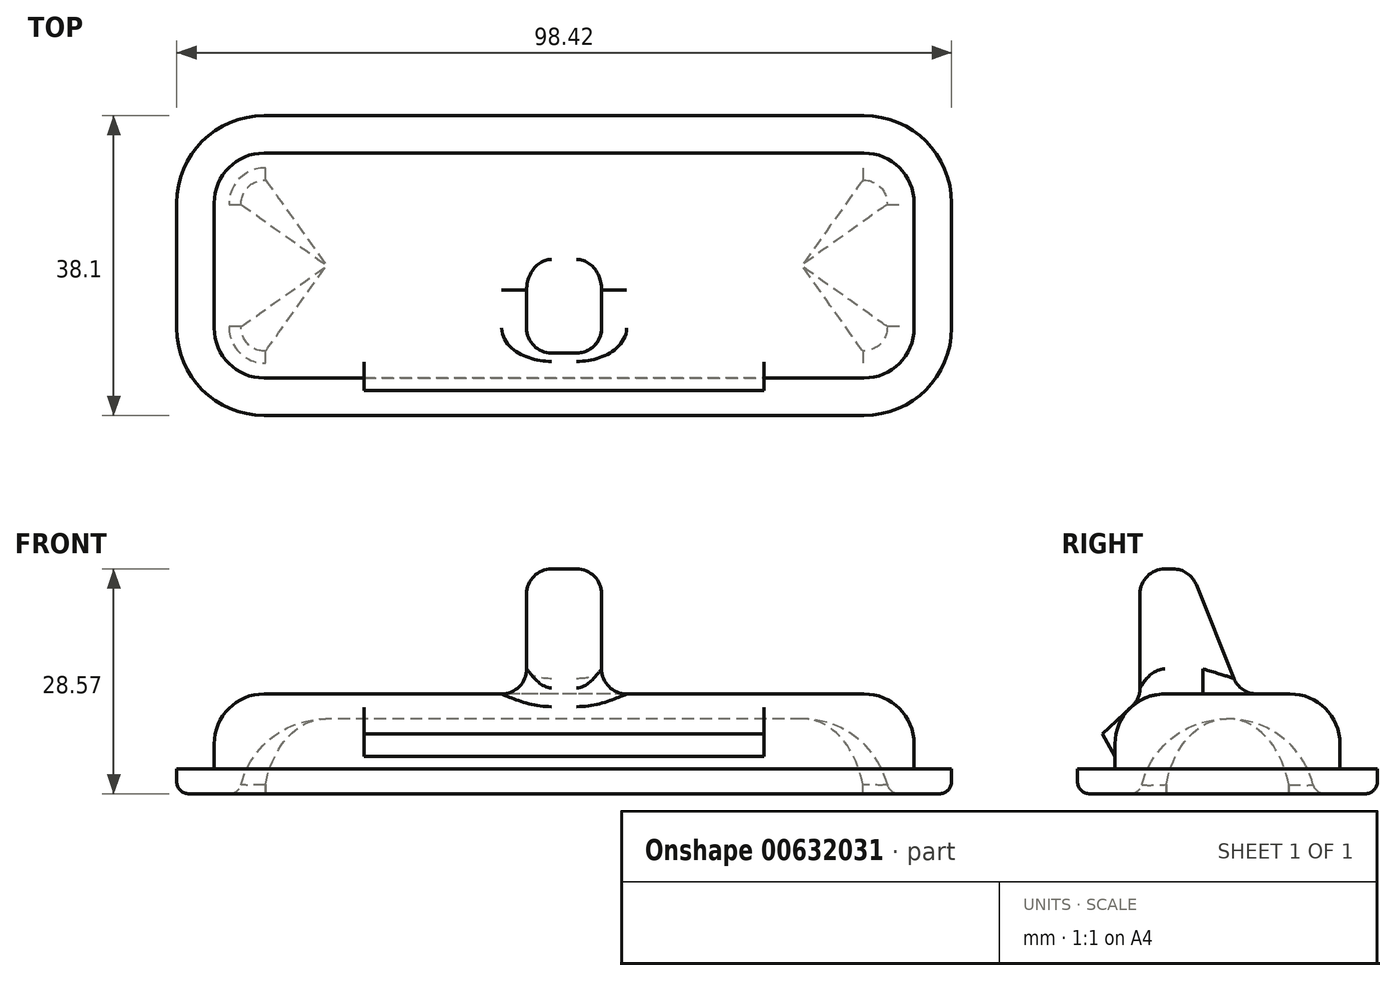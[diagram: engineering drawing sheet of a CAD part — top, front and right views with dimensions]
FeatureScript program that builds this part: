
annotation { "Feature Type Name" : "Feature", "Feature Type Description" : "" }
export const myFeature = defineFeature(function(context is Context, id is Id, definition is map)
    precondition{}
    {
        {
            var Q0;
            Q0=qCreatedBy(makeId("Top.planeOp"),FACE);
            var sketch = newSketch(context, id + "F0", { "sketchPlane" : qUnion([Q0])});
            skLineSegment(sketch, "E0.bottom", {"start": v(49.21, 19.05) * mm, "end": v(-49.21, 19.05) * mm});
            skLineSegment(sketch, "E0.top", {"start": v(49.21, -19.05) * mm, "end": v(-49.21, -19.05) * mm});
            skLineSegment(sketch, "E0.left", {"start": v(49.21, 19.05) * mm, "end": v(49.21, -19.05) * mm});
            skLineSegment(sketch, "E0.right", {"start": v(-49.21, 19.05) * mm, "end": v(-49.21, -19.05) * mm});
            skPoint(sketch, "E0.middle", {"position": v(0, 0) * mm});
            skSolve(sketch);
        }
        {
            var Q0;
            Q0=makeQuery(id+"F0.imprint","IMPRINT",FACE,{"disambiguationData":[TD([[makeQuery(id+"F0.imprint","IMPRINT",EDGE,{"derivedFrom":sQuery(id+"F0.wireOp",EDGE,"E0.bottom")}),1.0]])]});
            extrude(context, id + "F1", {"entities" : qUnion([Q0]), "depth" : 3.17 * mm, "offsetDistance" : 25.4 * mm});
        }
        {
            var Q0;
            Q0=makeQuery(id+"F1.opExtrude","CAP_FACE",FACE,{"disambiguationData":[OSD([sQuery(id+"F0.wireOp",EDGE,"E0.bottom"),sQuery(id+"F0.wireOp",EDGE,"E0.top"),sQuery(id+"F0.wireOp",EDGE,"E0.left"),sQuery(id+"F0.wireOp",EDGE,"E0.right")])],"isStart":false});
            var sketch = newSketch(context, id + "F2", { "sketchPlane" : qUnion([Q0])});
            skLineSegment(sketch, "E1.bottom", {"start": v(44.45, 14.29) * mm, "end": v(-44.45, 14.29) * mm});
            skLineSegment(sketch, "E1.top", {"start": v(44.45, -14.29) * mm, "end": v(-44.45, -14.29) * mm});
            skLineSegment(sketch, "E1.left", {"start": v(44.45, 14.29) * mm, "end": v(44.45, -14.29) * mm});
            skLineSegment(sketch, "E1.right", {"start": v(-44.45, 14.29) * mm, "end": v(-44.45, -14.29) * mm});
            skPoint(sketch, "E1.middle", {"position": v(0, 0) * mm});
            skSolve(sketch);
        }
        {
            var Q0;
            Q0=makeQuery(id+"F2.imprint","IMPRINT",FACE,{"disambiguationData":[TD([[makeQuery(id+"F2.imprint","IMPRINT",EDGE,{"derivedFrom":sQuery(id+"F2.wireOp",EDGE,"E1.bottom")}),1.0]])]});
            extrude(context, id + "F3", {"entities" : qUnion([Q0]), "operationType" : NewBodyOperationType.ADD, "depth" : 9.52 * mm, "offsetDistance" : 25.4 * mm});
        }
        {
            var Q0;
            Q0=makeQuery(id+"F1.opExtrude","SWEPT_EDGE",EDGE,{"disambiguationData":[OSD([sQuery(id+"F0.wireOp",EDGE,"E0.bottom"),sQuery(id+"F0.wireOp",EDGE,"E0.left")])]});
            var Q1;
            Q1=makeQuery(id+"F1.opExtrude","SWEPT_EDGE",EDGE,{"disambiguationData":[OSD([sQuery(id+"F0.wireOp",EDGE,"E0.top"),sQuery(id+"F0.wireOp",EDGE,"E0.left")])]});
            var Q2;
            Q2=makeQuery(id+"F1.opExtrude","SWEPT_EDGE",EDGE,{"disambiguationData":[OSD([sQuery(id+"F0.wireOp",EDGE,"E0.top"),sQuery(id+"F0.wireOp",EDGE,"E0.right")])]});
            var Q3;
            Q3=makeQuery(id+"F1.opExtrude","SWEPT_EDGE",EDGE,{"disambiguationData":[OSD([sQuery(id+"F0.wireOp",EDGE,"E0.bottom"),sQuery(id+"F0.wireOp",EDGE,"E0.right")])]});
            fillet(context, id + "F4", {"entities" : qUnion([Q0, Q1, Q2, Q3]), "radius" : 11.1 * mm, "tangentPropagation" : true, "allowEdgeOverflow" : false});
        }
        {
            var Q0;
            Q0=makeQuery(id+"F3.opExtrude","SWEPT_EDGE",EDGE,{"disambiguationData":[OSD([sQuery(id+"F2.wireOp",EDGE,"E1.top"),sQuery(id+"F2.wireOp",EDGE,"E1.left")])]});
            var Q1;
            Q1=makeQuery(id+"F3.opExtrude","SWEPT_EDGE",EDGE,{"disambiguationData":[OSD([sQuery(id+"F2.wireOp",EDGE,"E1.bottom"),sQuery(id+"F2.wireOp",EDGE,"E1.left")])]});
            var Q2;
            Q2=makeQuery(id+"F3.opExtrude","SWEPT_EDGE",EDGE,{"disambiguationData":[OSD([sQuery(id+"F2.wireOp",EDGE,"E1.bottom"),sQuery(id+"F2.wireOp",EDGE,"E1.right")])]});
            var Q3;
            Q3=makeQuery(id+"F3.opExtrude","SWEPT_EDGE",EDGE,{"disambiguationData":[OSD([sQuery(id+"F2.wireOp",EDGE,"E1.top"),sQuery(id+"F2.wireOp",EDGE,"E1.right")])]});
            fillet(context, id + "F5", {"entities" : qUnion([Q0, Q1, Q2, Q3]), "radius" : 6.35 * mm, "tangentPropagation" : true, "allowEdgeOverflow" : false});
        }
        {
            var Q0;
            Q0=makeQuery(id+"F1.opExtrude","CAP_FACE",FACE,{"disambiguationData":[OSD([sQuery(id+"F0.wireOp",EDGE,"E0.bottom"),sQuery(id+"F0.wireOp",EDGE,"E0.top"),sQuery(id+"F0.wireOp",EDGE,"E0.left"),sQuery(id+"F0.wireOp",EDGE,"E0.right")])],"isStart":true});
            shell(context, id + "F6", {"entities" : qUnion([Q0]), "thickness" : 3.17 * mm});
        }
        {
            var Q0;
            Q0=makeQuery(id+"F3.opExtrude","CAP_EDGE",EDGE,{"disambiguationData":[OSD([sQuery(id+"F2.wireOp",EDGE,"E1.top")])],"isStart":false});
            fillet(context, id + "F7", {"entities" : qUnion([Q0]), "radius" : 6.35 * mm, "tangentPropagation" : true, "allowEdgeOverflow" : false});
        }
        {
            var Q0;
            Q0=qCreatedBy(makeId("Right.planeOp"),FACE);
            var sketch = newSketch(context, id + "F8", { "sketchPlane" : qUnion([Q0])});
            skLineSegment(sketch, "E2", {"start": v(1.59, 12.7) * mm, "end": v(-4.76, 28.58) * mm});
            skLineSegment(sketch, "E3", {"start": v(-4.76, 28.58) * mm, "end": v(-11.11, 28.58) * mm});
            skLineSegment(sketch, "E4", {"start": v(-11.11, 11.85) * mm, "end": v(-11.11, 28.58) * mm});
            skArc(sketch, "E5.0", {"start": v(-7.94, 12.7) * mm, "mid": v(-9.58, 12.48) * mm, "end": v(-11.11, 11.85) * mm});
            skLineSegment(sketch, "E6.0", {"start": v(-7.94, 12.7) * mm, "end": v(1.59, 12.7) * mm});
            skPoint(sketch, "E7.orphan", {"position": v(-14.29, 6.35) * mm});
            skPoint(sketch, "E8.orphan", {"position": v(7.94, 12.7) * mm});
            skSolve(sketch);
        }
        {
            var Q0;
            Q0=qCreatedBy(makeId("Right.planeOp"),FACE);
            var sketch = newSketch(context, id + "F9", { "sketchPlane" : qUnion([Q0])});
            skLineSegment(sketch, "E9.0", {"start": v(-14.29, 3.18) * mm, "end": v(-14.29, 6.35) * mm});
            skLineSegment(sketch, "E10", {"start": v(-14.29, 4.76) * mm, "end": v(-15.88, 7.62) * mm});
            skLineSegment(sketch, "E11", {"start": v(-15.88, 7.62) * mm, "end": v(-15.88, 7.62) * mm});
            skLineSegment(sketch, "E12", {"start": v(-15.88, 7.62) * mm, "end": v(-12.28, 10.99) * mm});
            skPoint(sketch, "E13", {"position": v(-14.29, 4.76) * mm});
            skLineSegment(sketch, "E14", {"start": v(-15.88, 7.62) * mm, "end": v(-15.88, 11.92) * mm, "construction": true});
            skArc(sketch, "E15.0", {"start": v(-7.94, 12.7) * mm, "mid": v(-12.43, 10.84) * mm, "end": v(-14.29, 6.35) * mm});
            skSolve(sketch);
        }
        {
            var Q0;
            {var subQ3=sQuery(id+"F9.wireOp",EDGE,"E10");Q0=makeQuery(id+"F9.imprint","IMPRINT",FACE,{"disambiguationData":[TD([[makeQuery(id+"F9.imprint","IMPRINT",EDGE,{"derivedFrom":subQ3}),-1.0]])]});}
            extrude(context, id + "F10", {"entities" : qUnion([Q0]), "operationType" : NewBodyOperationType.ADD, "endBound" : BoundingType.SYMMETRIC, "oppositeDirection" : true, "depth" : 50.8 * mm, "offsetDistance" : 25.4 * mm});
        }
        {
            var Q0;
            Q0=makeQuery(id+"F8.imprint","IMPRINT",FACE,{"disambiguationData":[TD([[makeQuery(id+"F8.imprint","IMPRINT",EDGE,{"derivedFrom":sQuery(id+"F8.wireOp",EDGE,"E2")}),1.0]])]});
            extrude(context, id + "F11", {"entities" : qUnion([Q0]), "operationType" : NewBodyOperationType.ADD, "endBound" : BoundingType.SYMMETRIC, "depth" : 9.52 * mm, "offsetDistance" : 25.4 * mm});
        }
        {
            var Q0;
            Q0=makeQuery(id+"F11.opExtrude","CAP_EDGE",EDGE,{"disambiguationData":[OSD([sQuery(id+"F8.wireOp",EDGE,"38d0f216-046f-402e-82b9-bbc7f268f269.0")])],"isStart":false});
            var Q1;
            Q1=makeQuery(id+"F11.opExtrude","CAP_EDGE",EDGE,{"disambiguationData":[OSD([sQuery(id+"F8.wireOp",EDGE,"bf6b2ea2-482b-47d7-b613-27e2f9b7d257.0")])],"isStart":false});
            var Q2;
            Q2=makeQuery(id+"F11.opExtrude","CAP_FACE",FACE,{"disambiguationData":[OSD([sQuery(id+"F8.wireOp",EDGE,"E2"),sQuery(id+"F8.wireOp",EDGE,"E3"),sQuery(id+"F8.wireOp",EDGE,"E4"),sQuery(id+"F8.wireOp",EDGE,"38d0f216-046f-402e-82b9-bbc7f268f269.0"),sQuery(id+"F8.wireOp",EDGE,"bf6b2ea2-482b-47d7-b613-27e2f9b7d257.0")])],"isStart":false});
            var Q3;
            Q3=makeQuery(id+"F11.opExtrude","SWEPT_FACE",FACE,{"disambiguationData":[OSD([sQuery(id+"F8.wireOp",EDGE,"E4")])]});
            var Q4;
            Q4=makeQuery(id+"F11.opExtrude","CAP_FACE",FACE,{"disambiguationData":[OSD([sQuery(id+"F8.wireOp",EDGE,"E2"),sQuery(id+"F8.wireOp",EDGE,"E3"),sQuery(id+"F8.wireOp",EDGE,"E4"),sQuery(id+"F8.wireOp",EDGE,"38d0f216-046f-402e-82b9-bbc7f268f269.0"),sQuery(id+"F8.wireOp",EDGE,"bf6b2ea2-482b-47d7-b613-27e2f9b7d257.0")])],"isStart":true});
            var Q5;
            Q5=makeQuery(id+"F11.opExtrude","SWEPT_FACE",FACE,{"disambiguationData":[OSD([sQuery(id+"F8.wireOp",EDGE,"E2")])]});
            fillet(context, id + "F12", {"entities" : qUnion([Q0, Q1, Q2, Q3, Q4, Q5]), "radius" : 3.17 * mm, "tangentPropagation" : true, "allowEdgeOverflow" : false});
        }
        {
            var Q0;
            Q0=makeQuery(id+"F6.opShell","OFFSET_FACE",FACE,{"disambiguationData":[OSD([sQuery(id+"F2.wireOp",EDGE,"E1.bottom"),sQuery(id+"F2.wireOp",EDGE,"E1.top"),sQuery(id+"F2.wireOp",EDGE,"E1.left"),sQuery(id+"F2.wireOp",EDGE,"E1.right")])]});
            fillet(context, id + "F13", {"entities" : qUnion([Q0]), "radius" : 11.1 * mm, "tangentPropagation" : true, "allowEdgeOverflow" : false});
        }
        {
            var Q0;
            {var subQ0=sQuery(id+"F2.wireOp",EDGE,"E1.top");Q0=makeQuery(id+"F13.opFillet","BLEND_EDGE",EDGE,{"disambiguationData":[OD(1.0)],"blendedFrom":[makeQuery(id+"F6.opShell","OFFSET_EDGE",EDGE,{"disambiguationData":[OSD([subQ0]),TDD([makeQuery(id+"F3.opExtrude","CAP_EDGE",EDGE,{"disambiguationData":[OSD([subQ0])],"isStart":false})])]}),makeQuery(id+"F1.opExtrude","CAP_FACE",FACE,{"disambiguationData":[OSD([sQuery(id+"F0.wireOp",EDGE,"E0.bottom"),sQuery(id+"F0.wireOp",EDGE,"E0.top"),sQuery(id+"F0.wireOp",EDGE,"E0.left"),sQuery(id+"F0.wireOp",EDGE,"E0.right")])],"isStart":true})],"blendedInto":[makeQuery(id+"F1.opExtrude","CAP_FACE",FACE,{"disambiguationData":[OSD([sQuery(id+"F0.wireOp",EDGE,"E0.bottom"),sQuery(id+"F0.wireOp",EDGE,"E0.top"),sQuery(id+"F0.wireOp",EDGE,"E0.left"),sQuery(id+"F0.wireOp",EDGE,"E0.right")])],"isStart":true})]});}
            var Q1;
            {var subQ0=sQuery(id+"F2.wireOp",EDGE,"E1.top");Q1=makeQuery(id+"F13.opFillet","BLEND_EDGE",EDGE,{"disambiguationData":[OD(0.0)],"blendedFrom":[makeQuery(id+"F6.opShell","OFFSET_EDGE",EDGE,{"disambiguationData":[OSD([subQ0]),TDD([makeQuery(id+"F3.opExtrude","CAP_EDGE",EDGE,{"disambiguationData":[OSD([subQ0])],"isStart":false})])]}),makeQuery(id+"F1.opExtrude","CAP_FACE",FACE,{"disambiguationData":[OSD([sQuery(id+"F0.wireOp",EDGE,"E0.bottom"),sQuery(id+"F0.wireOp",EDGE,"E0.top"),sQuery(id+"F0.wireOp",EDGE,"E0.left"),sQuery(id+"F0.wireOp",EDGE,"E0.right")])],"isStart":true})],"blendedInto":[makeQuery(id+"F1.opExtrude","CAP_FACE",FACE,{"disambiguationData":[OSD([sQuery(id+"F0.wireOp",EDGE,"E0.bottom"),sQuery(id+"F0.wireOp",EDGE,"E0.top"),sQuery(id+"F0.wireOp",EDGE,"E0.left"),sQuery(id+"F0.wireOp",EDGE,"E0.right")])],"isStart":true})]});}
            var Q2;
            Q2=makeQuery(id+"F1.opExtrude","CAP_FACE",FACE,{"disambiguationData":[OSD([sQuery(id+"F0.wireOp",EDGE,"E0.bottom"),sQuery(id+"F0.wireOp",EDGE,"E0.top"),sQuery(id+"F0.wireOp",EDGE,"E0.left"),sQuery(id+"F0.wireOp",EDGE,"E0.right")])],"isStart":true});
            fillet(context, id + "F14", {"entities" : qUnion([Q0, Q1, Q2]), "radius" : 1.59 * mm, "tangentPropagation" : true, "allowEdgeOverflow" : false});
        }
    });
